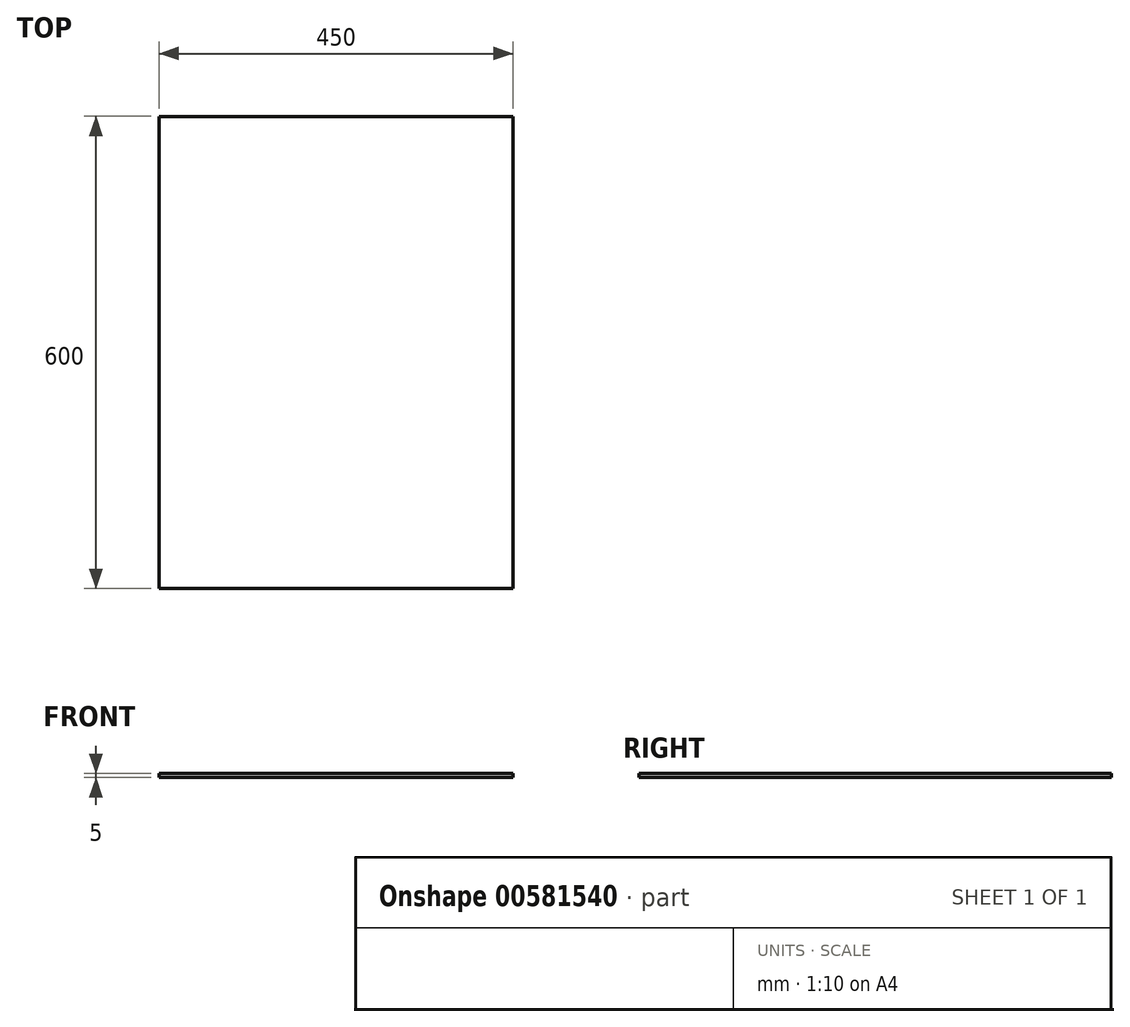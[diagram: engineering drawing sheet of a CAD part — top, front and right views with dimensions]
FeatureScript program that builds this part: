
annotation { "Feature Type Name" : "Feature", "Feature Type Description" : "" }
export const myFeature = defineFeature(function(context is Context, id is Id, definition is map)
    precondition{}
    {
        {
            var Q0;
            Q0=qCreatedBy(makeId("Top.planeOp"),FACE);
            var sketch = newSketch(context, id + "F0", { "sketchPlane" : qUnion([Q0])});
            skLineSegment(sketch, "E0.bottom", {"start": v(-413.62, 590.66) * mm, "end": v(36.38, 590.66) * mm});
            skLineSegment(sketch, "E0.top", {"start": v(-413.62, -9.34) * mm, "end": v(36.38, -9.34) * mm});
            skLineSegment(sketch, "E0.left", {"start": v(-413.62, 590.66) * mm, "end": v(-413.62, -9.34) * mm});
            skLineSegment(sketch, "E0.right", {"start": v(36.38, 590.66) * mm, "end": v(36.38, -9.34) * mm});
            skSolve(sketch);
        }
        {
            var Q0;
            Q0=makeQuery(id+"F0.imprint","IMPRINT",FACE,{"disambiguationData":[TD([[makeQuery(id+"F0.imprint","IMPRINT",EDGE,{"derivedFrom":sQuery(id+"F0.wireOp",EDGE,"E0.bottom")}),-1.0]])]});
            extrude(context, id + "F1", {"entities" : qUnion([Q0]), "depth" : 5 * mm, "offsetDistance" : 25 * mm});
        }
    });
